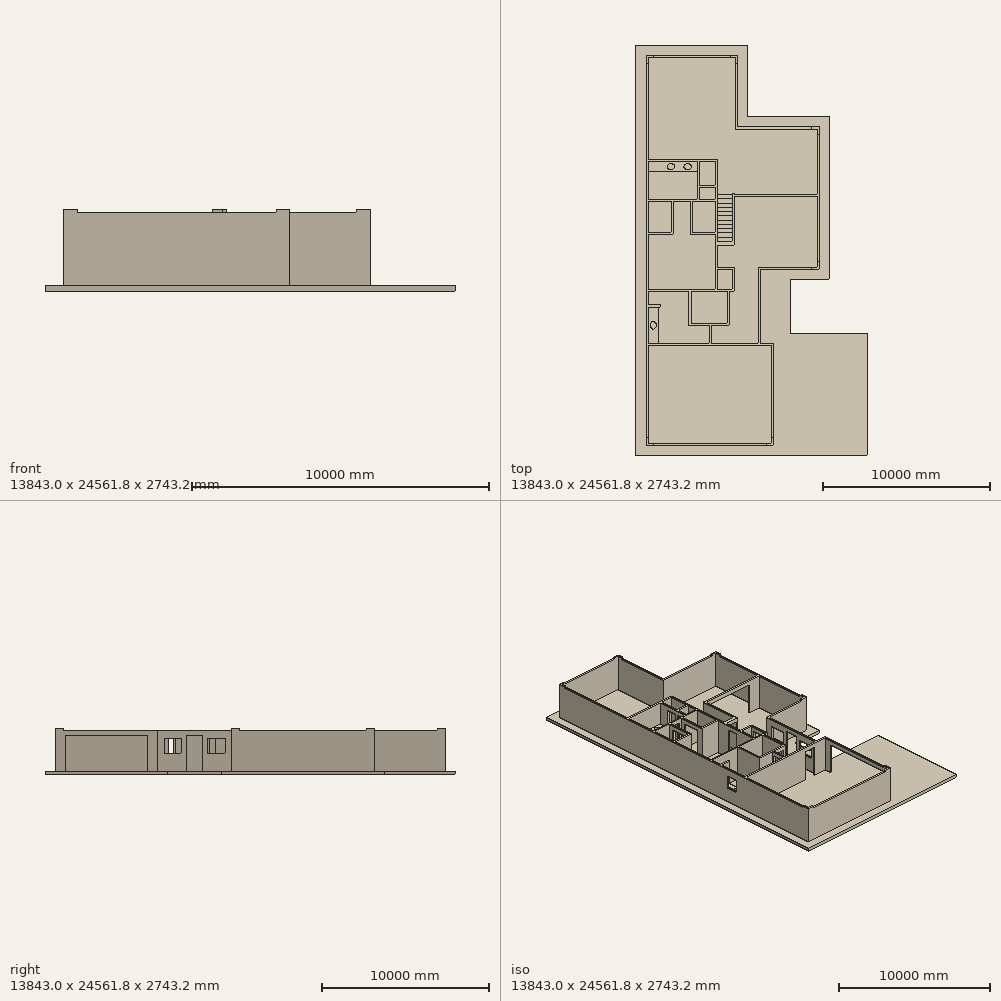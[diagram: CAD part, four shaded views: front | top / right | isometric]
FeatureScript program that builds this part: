
annotation { "Feature Type Name" : "Feature", "Feature Type Description" : "" }
export const myFeature = defineFeature(function(context is Context, id is Id, definition is map)
    precondition{}
    {
        {
            var Q0;
            Q0=qCreatedBy(makeId("Top.planeOp"),FACE);
            var sketch = newSketch(context, id + "F0", { "sketchPlane" : qUnion([Q0])});
            skLineSegment(sketch, "E0", {"start": v(0, 0) * mm, "end": v(7645.4, 0) * mm});
            skLineSegment(sketch, "E1", {"start": v(7645.4, 0) * mm, "end": v(7645.4, 6096) * mm});
            skLineSegment(sketch, "E2", {"start": v(7645.4, 6096) * mm, "end": v(6832.6, 6096) * mm});
            skLineSegment(sketch, "E3", {"start": v(6832.6, 6096) * mm, "end": v(6832.6, 10541) * mm});
            skLineSegment(sketch, "E4", {"start": v(6832.6, 10541) * mm, "end": v(10363.2, 10541) * mm});
            skLineSegment(sketch, "E5", {"start": v(10363.2, 10541) * mm, "end": v(10363.2, 19075.4) * mm});
            skLineSegment(sketch, "E6", {"start": v(10363.2, 19075.4) * mm, "end": v(5486.4, 19075.4) * mm});
            skLineSegment(sketch, "E7", {"start": v(5486.4, 19075.4) * mm, "end": v(5486.4, 23342.6) * mm});
            skLineSegment(sketch, "E8", {"start": v(5486.4, 23342.6) * mm, "end": v(0, 23342.6) * mm});
            skLineSegment(sketch, "E9", {"start": v(0, 23342.6) * mm, "end": v(0, 0) * mm});
            skSolve(sketch);
        }
        {
            var Q0;
            Q0=qSketchRegion(id+"F0",true);
            extrude(context, id + "F1", {"entities" : qUnion([Q0]), "depth" : 2641.6 * mm});
        }
        {
            var Q0;
            Q0=qCreatedBy(makeId("Top.planeOp"),FACE);
            var sketch = newSketch(context, id + "F2", { "sketchPlane" : qUnion([Q0])});
            skLineSegment(sketch, "E10", {"start": v(-609.6, 23952.2) * mm, "end": v(-609.6, -609.6) * mm});
            skLineSegment(sketch, "E11", {"start": v(-609.6, -609.6) * mm, "end": v(13233.4, -609.6) * mm});
            skLineSegment(sketch, "E12", {"start": v(13233.4, -609.6) * mm, "end": v(13233.4, 6705.6) * mm});
            skLineSegment(sketch, "E13", {"start": v(13233.4, 6705.6) * mm, "end": v(8661.4, 6705.6) * mm});
            skLineSegment(sketch, "E14", {"start": v(8661.4, 6705.6) * mm, "end": v(8661.4, 9931.4) * mm});
            skLineSegment(sketch, "E15", {"start": v(8661.4, 9931.4) * mm, "end": v(10972.8, 9931.4) * mm});
            skLineSegment(sketch, "E16", {"start": v(10972.8, 9931.4) * mm, "end": v(10972.8, 19685) * mm});
            skLineSegment(sketch, "E17", {"start": v(10972.8, 19685) * mm, "end": v(6096, 19685) * mm});
            skLineSegment(sketch, "E18", {"start": v(6096, 19685) * mm, "end": v(6096, 23952.2) * mm});
            skLineSegment(sketch, "E19", {"start": v(6096, 23952.2) * mm, "end": v(-609.6, 23952.2) * mm});
            skSolve(sketch);
        }
        {
            var Q0;
            Q0=qSketchRegion(id+"F2",true);
            extrude(context, id + "F3", {"entities" : qUnion([Q0]), "operationType" : NewBodyOperationType.ADD, "depth" : 203.2 * mm});
        }
        {
            var Q0;
            Q0=makeQuery(id+"F1.opExtrude","CAP_FACE",FACE,{"disambiguationData":[OSD([sQuery(id+"F0.wireOp",EDGE,"E0"),sQuery(id+"F0.wireOp",EDGE,"E1"),sQuery(id+"F0.wireOp",EDGE,"E2"),sQuery(id+"F0.wireOp",EDGE,"E3"),sQuery(id+"F0.wireOp",EDGE,"E4"),sQuery(id+"F0.wireOp",EDGE,"E5"),sQuery(id+"F0.wireOp",EDGE,"E6"),sQuery(id+"F0.wireOp",EDGE,"E7"),sQuery(id+"F0.wireOp",EDGE,"E8"),sQuery(id+"F0.wireOp",EDGE,"E9")])],"isStart":false});
            var sketch = newSketch(context, id + "F4", { "sketchPlane" : qUnion([Q0])});
            skLineSegment(sketch, "E20.bottom", {"start": v(127, 23215.6) * mm, "end": v(5359.4, 23215.6) * mm});
            skLineSegment(sketch, "E20.left", {"start": v(127, 23215.6) * mm, "end": v(127, 17119.6) * mm});
            skLineSegment(sketch, "E20.right", {"start": v(5359.4, 23215.6) * mm, "end": v(5359.4, 18948.4) * mm});
            skLineSegment(sketch, "E21.bottom", {"start": v(127, 5969) * mm, "end": v(7518.4, 5969) * mm});
            skLineSegment(sketch, "E21.top", {"start": v(127, 127) * mm, "end": v(7518.4, 127) * mm});
            skLineSegment(sketch, "E21.left", {"start": v(127, 5969) * mm, "end": v(127, 127) * mm});
            skLineSegment(sketch, "E21.right", {"start": v(7518.4, 5969) * mm, "end": v(7518.4, 127) * mm});
            skLineSegment(sketch, "E22", {"start": v(5359.4, 18948.4) * mm, "end": v(10236.2, 18948.4) * mm});
            skLineSegment(sketch, "E23", {"start": v(127, 17119.6) * mm, "end": v(4267.2, 17119.6) * mm});
            skLineSegment(sketch, "E24", {"start": v(4267.2, 17119.6) * mm, "end": v(4267.2, 10668) * mm});
            skLineSegment(sketch, "E25", {"start": v(4267.2, 10668) * mm, "end": v(5308.6, 10668) * mm});
            skLineSegment(sketch, "E26", {"start": v(10236.2, 10668) * mm, "end": v(10236.2, 14884.4) * mm});
            skLineSegment(sketch, "E27", {"start": v(5181.6, 15062.2) * mm, "end": v(5181.6, 11963.4) * mm});
            skLineSegment(sketch, "E28", {"start": v(5181.6, 11963.4) * mm, "end": v(5308.6, 11963.4) * mm});
            skLineSegment(sketch, "E29", {"start": v(5308.6, 11963.4) * mm, "end": v(5308.6, 14884.4) * mm});
            skLineSegment(sketch, "E30", {"start": v(5308.6, 14884.4) * mm, "end": v(10236.2, 14884.4) * mm});
            skLineSegment(sketch, "E31", {"start": v(5181.6, 15062.2) * mm, "end": v(5308.6, 15062.2) * mm});
            skLineSegment(sketch, "E32", {"start": v(5308.6, 15062.2) * mm, "end": v(5308.6, 15011.4) * mm});
            skLineSegment(sketch, "E33", {"start": v(5308.6, 15011.4) * mm, "end": v(10236.2, 15011.4) * mm});
            skLineSegment(sketch, "E34.trimOffspring", {"start": v(10236.2, 15011.4) * mm, "end": v(10236.2, 18948.4) * mm});
            skLineSegment(sketch, "E35.bottom", {"start": v(4140.2, 16992.6) * mm, "end": v(3225.8, 16992.6) * mm});
            skLineSegment(sketch, "E35.top", {"start": v(4140.2, 15570.2) * mm, "end": v(3225.8, 15570.2) * mm});
            skLineSegment(sketch, "E35.left", {"start": v(4140.2, 16992.6) * mm, "end": v(4140.2, 15570.2) * mm});
            skLineSegment(sketch, "E35.right", {"start": v(3225.8, 16992.6) * mm, "end": v(3225.8, 15570.2) * mm});
            skLineSegment(sketch, "E36.bottom", {"start": v(127, 16992.6) * mm, "end": v(3098.8, 16992.6) * mm});
            skLineSegment(sketch, "E36.top", {"start": v(127, 14706.6) * mm, "end": v(3098.8, 14706.6) * mm});
            skLineSegment(sketch, "E36.left", {"start": v(127, 16992.6) * mm, "end": v(127, 14706.6) * mm});
            skLineSegment(sketch, "E36.right", {"start": v(3098.8, 16992.6) * mm, "end": v(3098.8, 14706.6) * mm});
            skLineSegment(sketch, "E37.bottom", {"start": v(127, 14579.6) * mm, "end": v(1498.6, 14579.6) * mm});
            skLineSegment(sketch, "E37.top", {"start": v(127, 12750.8) * mm, "end": v(1498.6, 12750.8) * mm});
            skLineSegment(sketch, "E37.left", {"start": v(127, 14579.6) * mm, "end": v(127, 12750.8) * mm});
            skLineSegment(sketch, "E37.right", {"start": v(1498.6, 14579.6) * mm, "end": v(1498.6, 12750.8) * mm});
            skLineSegment(sketch, "E38.bottom", {"start": v(2768.6, 14579.6) * mm, "end": v(4140.2, 14579.6) * mm});
            skLineSegment(sketch, "E38.top", {"start": v(2768.6, 12750.8) * mm, "end": v(4140.2, 12750.8) * mm});
            skLineSegment(sketch, "E38.left", {"start": v(2768.6, 14579.6) * mm, "end": v(2768.6, 12750.8) * mm});
            skLineSegment(sketch, "E38.right", {"start": v(4140.2, 14579.6) * mm, "end": v(4140.2, 12750.8) * mm});
            skLineSegment(sketch, "E39", {"start": v(2641.6, 12623.8) * mm, "end": v(2641.6, 14579.6) * mm});
            skLineSegment(sketch, "E40", {"start": v(2641.6, 14579.6) * mm, "end": v(1625.6, 14579.6) * mm});
            skLineSegment(sketch, "E41", {"start": v(1625.6, 14579.6) * mm, "end": v(1625.6, 12623.8) * mm});
            skLineSegment(sketch, "E42", {"start": v(1625.6, 12623.8) * mm, "end": v(127, 12623.8) * mm});
            skLineSegment(sketch, "E43", {"start": v(2641.6, 12623.8) * mm, "end": v(4140.2, 12623.8) * mm});
            skLineSegment(sketch, "E44.bottom", {"start": v(4267.2, 10541) * mm, "end": v(5181.6, 10541) * mm});
            skLineSegment(sketch, "E44.top", {"start": v(4267.2, 9321.8) * mm, "end": v(5181.6, 9321.8) * mm});
            skLineSegment(sketch, "E44.left", {"start": v(4267.2, 10541) * mm, "end": v(4267.2, 9321.8) * mm});
            skLineSegment(sketch, "E44.right", {"start": v(5181.6, 10541) * mm, "end": v(5181.6, 9321.8) * mm});
            skLineSegment(sketch, "E45.right", {"start": v(2692.4, 9194.8) * mm, "end": v(2692.4, 7289.8) * mm});
            skLineSegment(sketch, "E46", {"start": v(4140.2, 12623.8) * mm, "end": v(4140.2, 9321.8) * mm});
            skLineSegment(sketch, "E47", {"start": v(4140.2, 9321.8) * mm, "end": v(127, 9321.8) * mm});
            skLineSegment(sketch, "E48", {"start": v(127, 9321.8) * mm, "end": v(127, 12623.8) * mm});
            skLineSegment(sketch, "E49", {"start": v(3784.6, 6096) * mm, "end": v(127, 6096) * mm});
            skLineSegment(sketch, "E50", {"start": v(127, 6096) * mm, "end": v(127, 8280.4) * mm});
            skLineSegment(sketch, "E51", {"start": v(127, 9194.8) * mm, "end": v(2565.4, 9194.8) * mm});
            skLineSegment(sketch, "E52", {"start": v(2565.4, 9194.8) * mm, "end": v(2565.4, 7162.8) * mm});
            skLineSegment(sketch, "E53", {"start": v(2565.4, 7162.8) * mm, "end": v(3784.6, 7162.8) * mm});
            skLineSegment(sketch, "E54", {"start": v(3784.6, 7162.8) * mm, "end": v(3784.6, 6096) * mm});
            skLineSegment(sketch, "E55", {"start": v(3911.6, 7162.8) * mm, "end": v(3911.6, 6096) * mm});
            skLineSegment(sketch, "E56", {"start": v(3911.6, 6096) * mm, "end": v(6705.6, 6096) * mm});
            skLineSegment(sketch, "E57", {"start": v(6705.6, 6096) * mm, "end": v(6705.6, 10668) * mm});
            skLineSegment(sketch, "E58", {"start": v(3911.6, 7162.8) * mm, "end": v(5003.8, 7162.8) * mm});
            skLineSegment(sketch, "E59", {"start": v(5308.6, 9194.8) * mm, "end": v(5308.6, 10668) * mm});
            skLineSegment(sketch, "E60.trimOffspring", {"start": v(6705.6, 10668) * mm, "end": v(10236.2, 10668) * mm});
            skLineSegment(sketch, "E61.bottom", {"start": v(3225.8, 15443.2) * mm, "end": v(4140.2, 15443.2) * mm});
            skLineSegment(sketch, "E61.top", {"start": v(3225.8, 14706.6) * mm, "end": v(4140.2, 14706.6) * mm});
            skLineSegment(sketch, "E61.left", {"start": v(3225.8, 15443.2) * mm, "end": v(3225.8, 14706.6) * mm});
            skLineSegment(sketch, "E61.right", {"start": v(4140.2, 15443.2) * mm, "end": v(4140.2, 14706.6) * mm});
            skLineSegment(sketch, "E62", {"start": v(127, 8407.4) * mm, "end": v(889, 8407.4) * mm});
            skLineSegment(sketch, "E63", {"start": v(889, 8407.4) * mm, "end": v(889, 8280.4) * mm});
            skLineSegment(sketch, "E64", {"start": v(889, 8280.4) * mm, "end": v(127, 8280.4) * mm});
            skLineSegment(sketch, "E65.trimOffspring", {"start": v(127, 8407.4) * mm, "end": v(127, 9194.8) * mm});
            skLineSegment(sketch, "E66", {"start": v(2692.4, 9194.8) * mm, "end": v(4876.8, 9194.8) * mm});
            skLineSegment(sketch, "E67", {"start": v(4876.8, 9194.8) * mm, "end": v(4876.8, 7289.8) * mm});
            skLineSegment(sketch, "E68", {"start": v(4876.8, 7289.8) * mm, "end": v(2692.4, 7289.8) * mm});
            skLineSegment(sketch, "E69", {"start": v(5003.8, 7162.8) * mm, "end": v(5003.8, 9194.8) * mm});
            skLineSegment(sketch, "E70", {"start": v(5003.8, 9194.8) * mm, "end": v(5308.6, 9194.8) * mm});
            skSolve(sketch);
        }
        {
            var Q0;
            Q0=qSketchRegion(id+"F4",true);
            extrude(context, id + "F5", {"entities" : qUnion([Q0]), "operationType" : NewBodyOperationType.REMOVE, "oppositeDirection" : true, "depth" : 2438.4 * mm});
        }
        {
            var Q0;
            Q0=makeQuery(id+"F5.boolean.opBoolean","COPY",FACE,{"derivedFrom":makeQuery(id+"F5.opExtrude","SWEPT_FACE",FACE,{"disambiguationData":[OSD([sQuery(id+"F4.wireOp",EDGE,"E24")])]})});
            var sketch = newSketch(context, id + "F6", { "sketchPlane" : qUnion([Q0])});
            skLineSegment(sketch, "E71", {"start": v(14757.4, 203.2) * mm, "end": v(15011.4, 203.2) * mm});
            skLineSegment(sketch, "E72", {"start": v(15011.4, 203.2) * mm, "end": v(15011.4, 406.4) * mm});
            skLineSegment(sketch, "E73", {"start": v(15011.4, 406.4) * mm, "end": v(14757.4, 406.4) * mm});
            skLineSegment(sketch, "E74", {"start": v(14757.4, 406.4) * mm, "end": v(14757.4, 609.6) * mm});
            skLineSegment(sketch, "E75", {"start": v(14757.4, 609.6) * mm, "end": v(14503.4, 609.6) * mm});
            skLineSegment(sketch, "E76", {"start": v(14503.4, 609.6) * mm, "end": v(14503.4, 812.8) * mm});
            skLineSegment(sketch, "E77", {"start": v(14503.4, 812.8) * mm, "end": v(14249.4, 812.8) * mm});
            skLineSegment(sketch, "E78", {"start": v(14249.4, 812.8) * mm, "end": v(14249.4, 1016) * mm});
            skLineSegment(sketch, "E79", {"start": v(14249.4, 1016) * mm, "end": v(13995.4, 1016) * mm});
            skLineSegment(sketch, "E80", {"start": v(13995.4, 1016) * mm, "end": v(13995.4, 1219.2) * mm});
            skLineSegment(sketch, "E81", {"start": v(13995.4, 1219.2) * mm, "end": v(13741.4, 1219.2) * mm});
            skLineSegment(sketch, "E82", {"start": v(13741.4, 1219.2) * mm, "end": v(13741.4, 1422.4) * mm});
            skLineSegment(sketch, "E83", {"start": v(13741.4, 1422.4) * mm, "end": v(13487.4, 1422.4) * mm});
            skLineSegment(sketch, "E84", {"start": v(13487.4, 1422.4) * mm, "end": v(13487.4, 1625.6) * mm});
            skLineSegment(sketch, "E85", {"start": v(13487.4, 1625.6) * mm, "end": v(13233.4, 1625.6) * mm});
            skLineSegment(sketch, "E86", {"start": v(13233.4, 1625.6) * mm, "end": v(13233.4, 1828.8) * mm});
            skLineSegment(sketch, "E87", {"start": v(13233.4, 1828.8) * mm, "end": v(12979.4, 1828.8) * mm});
            skLineSegment(sketch, "E88", {"start": v(12979.4, 1828.8) * mm, "end": v(12979.4, 2032) * mm});
            skLineSegment(sketch, "E89", {"start": v(12979.4, 2032) * mm, "end": v(12725.4, 2032) * mm});
            skLineSegment(sketch, "E90", {"start": v(12725.4, 2032) * mm, "end": v(12725.4, 2235.2) * mm});
            skLineSegment(sketch, "E91", {"start": v(12725.4, 2235.2) * mm, "end": v(12471.4, 2235.2) * mm});
            skLineSegment(sketch, "E92", {"start": v(12471.4, 2235.2) * mm, "end": v(12471.4, 2438.4) * mm});
            skLineSegment(sketch, "E93", {"start": v(12471.4, 2438.4) * mm, "end": v(12217.4, 2438.4) * mm});
            skLineSegment(sketch, "E94", {"start": v(12217.4, 2438.4) * mm, "end": v(12217.4, 2641.6) * mm});
            skLineSegment(sketch, "E95", {"start": v(12217.4, 2641.6) * mm, "end": v(11963.4, 2641.6) * mm});
            skLineSegment(sketch, "E96", {"start": v(11963.4, 2641.6) * mm, "end": v(11963.4, 2387.6) * mm});
            skLineSegment(sketch, "E97", {"start": v(11963.4, 2387.6) * mm, "end": v(14757.4, 203.2) * mm});
            skSolve(sketch);
        }
        {
            var Q0;
            Q0=qSketchRegion(id+"F6",true);
            extrude(context, id + "F7", {"entities" : qUnion([Q0]), "operationType" : NewBodyOperationType.ADD, "endBound" : BoundingType.UP_TO_NEXT, "depth" : 25.4 * mm});
        }
        {
            var Q0;
            Q0=makeQuery(id+"F5.boolean.opBoolean","COPY",FACE,{"derivedFrom":makeQuery(id+"F5.opExtrude","SWEPT_FACE",FACE,{"disambiguationData":[OSD([sQuery(id+"F4.wireOp",EDGE,"E21.right")])]})});
            var sketch = newSketch(context, id + "F8", { "sketchPlane" : qUnion([Q0])});
            skLineSegment(sketch, "E98.bottom", {"start": v(-5486.4, 203.2) * mm, "end": v(-609.6, 203.2) * mm});
            skLineSegment(sketch, "E98.top", {"start": v(-5486.4, 2336.8) * mm, "end": v(-609.6, 2336.8) * mm});
            skLineSegment(sketch, "E98.left", {"start": v(-5486.4, 203.2) * mm, "end": v(-5486.4, 2336.8) * mm});
            skLineSegment(sketch, "E98.right", {"start": v(-609.6, 203.2) * mm, "end": v(-609.6, 2336.8) * mm});
            skLineSegment(sketch, "E99", {"start": v(-3048, 2641.6) * mm, "end": v(-3048, 203.2) * mm, "construction": true});
            skSolve(sketch);
        }
        {
            var Q0;
            Q0=qSketchRegion(id+"F8",true);
            extrude(context, id + "F9", {"entities" : qUnion([Q0]), "operationType" : NewBodyOperationType.REMOVE, "endBound" : BoundingType.UP_TO_NEXT, "oppositeDirection" : true, "depth" : 25.4 * mm});
        }
        {
            var Q0;
            Q0=makeQuery(id+"F5.boolean.opBoolean","COPY",FACE,{"derivedFrom":makeQuery(id+"F5.opExtrude","SWEPT_FACE",FACE,{"disambiguationData":[OSD([sQuery(id+"F4.wireOp",EDGE,"E30")])]})});
            var sketch = newSketch(context, id + "F10", { "sketchPlane" : qUnion([Q0])});
            skLineSegment(sketch, "E100.bottom", {"start": v(5461, 203.2) * mm, "end": v(9372.6, 203.2) * mm});
            skLineSegment(sketch, "E100.top", {"start": v(5461, 2336.8) * mm, "end": v(9372.6, 2336.8) * mm});
            skLineSegment(sketch, "E100.left", {"start": v(5461, 203.2) * mm, "end": v(5461, 2336.8) * mm});
            skLineSegment(sketch, "E100.right", {"start": v(9372.6, 203.2) * mm, "end": v(9372.6, 2336.8) * mm});
            skSolve(sketch);
        }
        {
            var Q0;
            Q0=qSketchRegion(id+"F10",true);
            extrude(context, id + "F11", {"entities" : qUnion([Q0]), "operationType" : NewBodyOperationType.REMOVE, "endBound" : BoundingType.UP_TO_NEXT, "oppositeDirection" : true, "depth" : 25.4 * mm});
        }
        {
            var Q0;
            Q0=makeQuery(id+"F5.boolean.opBoolean","COPY",FACE,{"derivedFrom":makeQuery(id+"F5.opExtrude","CAP_FACE",FACE,{"disambiguationData":[OSD([sQuery(id+"F4.wireOp",EDGE,"E36.bottom"),sQuery(id+"F4.wireOp",EDGE,"E36.top"),sQuery(id+"F4.wireOp",EDGE,"E36.left"),sQuery(id+"F4.wireOp",EDGE,"E36.right")])],"isStart":false})});
            var sketch = newSketch(context, id + "F12", { "sketchPlane" : qUnion([Q0])});
            skLineSegment(sketch, "E101.bottom", {"start": v(127, 16992.6) * mm, "end": v(3098.8, 16992.6) * mm});
            skLineSegment(sketch, "E101.top", {"start": v(127, 16383) * mm, "end": v(3098.8, 16383) * mm});
            skLineSegment(sketch, "E101.left", {"start": v(127, 16992.6) * mm, "end": v(127, 16383) * mm});
            skLineSegment(sketch, "E101.right", {"start": v(3098.8, 16992.6) * mm, "end": v(3098.8, 16383) * mm});
            skSolve(sketch);
        }
        {
            var Q0;
            Q0=qSketchRegion(id+"F12",true);
            extrude(context, id + "F13", {"entities" : qUnion([Q0]), "operationType" : NewBodyOperationType.ADD, "depth" : 838.2 * mm});
        }
        {
            var Q0;
            Q0=makeQuery(id+"F13.opExtrude","CAP_FACE",FACE,{"disambiguationData":[OSD([sQuery(id+"F12.wireOp",EDGE,"E101.bottom"),sQuery(id+"F12.wireOp",EDGE,"E101.top"),sQuery(id+"F12.wireOp",EDGE,"E101.left"),sQuery(id+"F12.wireOp",EDGE,"E101.right")])],"isStart":false});
            var sketch = newSketch(context, id + "F14", { "sketchPlane" : qUnion([Q0])});
            skLineSegment(sketch, "E102", {"start": v(2489.2, 16992.6) * mm, "end": v(2489.2, 16383) * mm, "construction": true});
            skLineSegment(sketch, "E103", {"start": v(1498.6, 16992.6) * mm, "end": v(1498.6, 16383) * mm, "construction": true});
            skEllipse(sketch, "E104", {"center": v(2489.2, 16687.8) * mm, "majorRadius": 228.6 * mm, "minorRadius": 177.8 * mm, "majorAxis": v(-1, 0)});
            skEllipse(sketch, "E105", {"center": v(1498.6, 16687.8) * mm, "majorRadius": 228.6 * mm, "minorRadius": 177.8 * mm, "majorAxis": v(-1, 0)});
            skSolve(sketch);
        }
        {
            var Q0;
            Q0=qSketchRegion(id+"F14",true);
            extrude(context, id + "F15", {"entities" : qUnion([Q0]), "operationType" : NewBodyOperationType.REMOVE, "oppositeDirection" : true, "depth" : 304.8 * mm});
        }
        {
            var Q0;
            Q0=makeQuery(id+"F5.boolean.opBoolean","COPY",FACE,{"derivedFrom":makeQuery(id+"F5.opExtrude","CAP_FACE",FACE,{"disambiguationData":[OSD([sQuery(id+"F4.wireOp",EDGE,"E49"),sQuery(id+"F4.wireOp",EDGE,"E50"),sQuery(id+"F4.wireOp",EDGE,"E51"),sQuery(id+"F4.wireOp",EDGE,"E52"),sQuery(id+"F4.wireOp",EDGE,"E53"),sQuery(id+"F4.wireOp",EDGE,"E54")])],"isStart":false})});
            var sketch = newSketch(context, id + "F16", { "sketchPlane" : qUnion([Q0])});
            skLineSegment(sketch, "E106.bottom", {"start": v(127, 6096) * mm, "end": v(736.6, 6096) * mm});
            skLineSegment(sketch, "E106.top", {"start": v(127, 8280.4) * mm, "end": v(736.6, 8280.4) * mm});
            skLineSegment(sketch, "E106.left", {"start": v(127, 6096) * mm, "end": v(127, 8280.4) * mm});
            skLineSegment(sketch, "E106.right", {"start": v(736.6, 6096) * mm, "end": v(736.6, 8280.4) * mm});
            skSolve(sketch);
        }
        {
            var Q0;
            Q0=qSketchRegion(id+"F16",true);
            extrude(context, id + "F17", {"entities" : qUnion([Q0]), "operationType" : NewBodyOperationType.ADD, "depth" : 838.2 * mm});
        }
        {
            var Q0;
            Q0=makeQuery(id+"F17.opExtrude","CAP_FACE",FACE,{"disambiguationData":[OSD([sQuery(id+"F16.wireOp",EDGE,"E106.bottom"),sQuery(id+"F16.wireOp",EDGE,"E106.top"),sQuery(id+"F16.wireOp",EDGE,"E106.left"),sQuery(id+"F16.wireOp",EDGE,"E106.right")])],"isStart":false});
            var sketch = newSketch(context, id + "F18", { "sketchPlane" : qUnion([Q0])});
            skLineSegment(sketch, "E107", {"start": v(127, 7188.2) * mm, "end": v(736.6, 7188.2) * mm, "construction": true});
            skEllipse(sketch, "E108", {"center": v(431.8, 7188.2) * mm, "majorRadius": 228.6 * mm, "minorRadius": 177.8 * mm, "majorAxis": v(0, 1)});
            skSolve(sketch);
        }
        {
            var Q0;
            Q0=qSketchRegion(id+"F18",true);
            extrude(context, id + "F19", {"entities" : qUnion([Q0]), "operationType" : NewBodyOperationType.REMOVE, "oppositeDirection" : true, "depth" : 304.8 * mm});
        }
        {
            var Q0;
            Q0=makeQuery(id+"F1.opExtrude","SWEPT_FACE",FACE,{"disambiguationData":[OSD([sQuery(id+"F0.wireOp",EDGE,"E3")])]});
            var sketch = newSketch(context, id + "F20", { "sketchPlane" : qUnion([Q0])});
            skLineSegment(sketch, "E109.bottom", {"start": v(7861.3, 203.2) * mm, "end": v(8775.7, 203.2) * mm});
            skLineSegment(sketch, "E109.top", {"start": v(7861.3, 2336.8) * mm, "end": v(8775.7, 2336.8) * mm});
            skLineSegment(sketch, "E109.left", {"start": v(7861.3, 203.2) * mm, "end": v(7861.3, 2336.8) * mm});
            skLineSegment(sketch, "E109.right", {"start": v(8775.7, 203.2) * mm, "end": v(8775.7, 2336.8) * mm});
            skLineSegment(sketch, "E110", {"start": v(8318.5, 2641.6) * mm, "end": v(8318.5, 203.2) * mm, "construction": true});
            skLineSegment(sketch, "E111.bottom", {"start": v(6489.7, 2159) * mm, "end": v(7556.5, 2159) * mm});
            skLineSegment(sketch, "E111.top", {"start": v(6489.7, 1244.6) * mm, "end": v(7556.5, 1244.6) * mm});
            skLineSegment(sketch, "E111.left", {"start": v(6489.7, 2159) * mm, "end": v(6489.7, 1244.6) * mm});
            skLineSegment(sketch, "E111.right", {"start": v(7556.5, 2159) * mm, "end": v(7556.5, 1244.6) * mm});
            skLineSegment(sketch, "E112.MirrorCS", {"start": v(10147.3, 2159) * mm, "end": v(9080.5, 2159) * mm});
            skLineSegment(sketch, "E113.MirrorCS", {"start": v(10147.3, 1244.6) * mm, "end": v(9080.5, 1244.6) * mm});
            skLineSegment(sketch, "E114.MirrorCS", {"start": v(10147.3, 2159) * mm, "end": v(10147.3, 1244.6) * mm});
            skLineSegment(sketch, "E115.MirrorCS", {"start": v(9080.5, 2159) * mm, "end": v(9080.5, 1244.6) * mm});
            skSolve(sketch);
        }
        {
            var Q0;
            Q0=qSketchRegion(id+"F20",true);
            extrude(context, id + "F21", {"entities" : qUnion([Q0]), "operationType" : NewBodyOperationType.REMOVE, "endBound" : BoundingType.UP_TO_NEXT, "oppositeDirection" : true, "depth" : 25.4 * mm});
        }
        {
            var Q0;
            Q0=makeQuery(id+"F5.boolean.opBoolean","COPY",FACE,{"derivedFrom":makeQuery(id+"F5.opExtrude","SWEPT_FACE",FACE,{"disambiguationData":[OSD([sQuery(id+"F4.wireOp",EDGE,"E56")])]})});
            var sketch = newSketch(context, id + "F22", { "sketchPlane" : qUnion([Q0])});
            skLineSegment(sketch, "E116.bottom", {"start": v(-6553.2, 203.2) * mm, "end": v(-5638.8, 203.2) * mm});
            skLineSegment(sketch, "E116.top", {"start": v(-6553.2, 2336.8) * mm, "end": v(-5638.8, 2336.8) * mm});
            skLineSegment(sketch, "E116.left", {"start": v(-6553.2, 203.2) * mm, "end": v(-6553.2, 2336.8) * mm});
            skLineSegment(sketch, "E116.right", {"start": v(-5638.8, 203.2) * mm, "end": v(-5638.8, 2336.8) * mm});
            skSolve(sketch);
        }
        {
            var Q0;
            Q0=qSketchRegion(id+"F22",true);
            extrude(context, id + "F23", {"entities" : qUnion([Q0]), "operationType" : NewBodyOperationType.REMOVE, "endBound" : BoundingType.UP_TO_NEXT, "oppositeDirection" : true, "depth" : 25.4 * mm});
        }
        {
            var Q0;
            Q0=makeQuery(id+"F5.boolean.opBoolean","COPY",FACE,{"derivedFrom":makeQuery(id+"F5.opExtrude","SWEPT_FACE",FACE,{"disambiguationData":[OSD([sQuery(id+"F4.wireOp",EDGE,"E58")])]})});
            var sketch = newSketch(context, id + "F24", { "sketchPlane" : qUnion([Q0])});
            skLineSegment(sketch, "E117.bottom", {"start": v(4013.2, 203.2) * mm, "end": v(4775.2, 203.2) * mm});
            skLineSegment(sketch, "E117.top", {"start": v(4013.2, 2336.8) * mm, "end": v(4775.2, 2336.8) * mm});
            skLineSegment(sketch, "E117.left", {"start": v(4013.2, 203.2) * mm, "end": v(4013.2, 2336.8) * mm});
            skLineSegment(sketch, "E117.right", {"start": v(4775.2, 203.2) * mm, "end": v(4775.2, 2336.8) * mm});
            skSolve(sketch);
        }
        {
            var Q0;
            Q0=qSketchRegion(id+"F24",true);
            extrude(context, id + "F25", {"entities" : qUnion([Q0]), "operationType" : NewBodyOperationType.REMOVE, "endBound" : BoundingType.UP_TO_NEXT, "oppositeDirection" : true, "depth" : 25.4 * mm});
        }
        {
            var Q0;
            Q0=makeQuery(id+"F5.boolean.opBoolean","COPY",FACE,{"derivedFrom":makeQuery(id+"F5.opExtrude","SWEPT_FACE",FACE,{"disambiguationData":[OSD([sQuery(id+"F4.wireOp",EDGE,"E55")])]})});
            var sketch = newSketch(context, id + "F26", { "sketchPlane" : qUnion([Q0])});
            skLineSegment(sketch, "E118.bottom", {"start": v(7048.5, 203.2) * mm, "end": v(6286.5, 203.2) * mm});
            skLineSegment(sketch, "E118.top", {"start": v(7048.5, 2336.8) * mm, "end": v(6286.5, 2336.8) * mm});
            skLineSegment(sketch, "E118.left", {"start": v(7048.5, 203.2) * mm, "end": v(7048.5, 2336.8) * mm});
            skLineSegment(sketch, "E118.right", {"start": v(6286.5, 203.2) * mm, "end": v(6286.5, 2336.8) * mm});
            skSolve(sketch);
        }
        {
            var Q0;
            Q0=qSketchRegion(id+"F26",true);
            extrude(context, id + "F27", {"entities" : qUnion([Q0]), "operationType" : NewBodyOperationType.REMOVE, "endBound" : BoundingType.UP_TO_NEXT, "oppositeDirection" : true, "depth" : 25.4 * mm});
        }
        {
            var Q0;
            Q0=makeQuery(id+"F5.boolean.opBoolean","COPY",FACE,{"derivedFrom":makeQuery(id+"F5.opExtrude","SWEPT_FACE",FACE,{"disambiguationData":[OSD([sQuery(id+"F4.wireOp",EDGE,"E50")])]})});
            var sketch = newSketch(context, id + "F28", { "sketchPlane" : qUnion([Q0])});
            skLineSegment(sketch, "E119.bottom", {"start": v(6731, 2159) * mm, "end": v(7645.4, 2159) * mm});
            skLineSegment(sketch, "E119.top", {"start": v(6731, 1244.6) * mm, "end": v(7645.4, 1244.6) * mm});
            skLineSegment(sketch, "E119.left", {"start": v(6731, 2159) * mm, "end": v(6731, 1244.6) * mm});
            skLineSegment(sketch, "E119.right", {"start": v(7645.4, 2159) * mm, "end": v(7645.4, 1244.6) * mm});
            skLineSegment(sketch, "E120", {"start": v(7188.2, 2641.6) * mm, "end": v(7188.2, 1041.4) * mm, "construction": true});
            skSolve(sketch);
        }
        {
            var Q0;
            Q0=qSketchRegion(id+"F28",true);
            extrude(context, id + "F29", {"entities" : qUnion([Q0]), "operationType" : NewBodyOperationType.REMOVE, "endBound" : BoundingType.UP_TO_NEXT, "oppositeDirection" : true, "depth" : 25.4 * mm});
        }
        {
            var Q0;
            Q0=makeQuery(id+"F5.boolean.opBoolean","COPY",FACE,{"derivedFrom":makeQuery(id+"F5.opExtrude","SWEPT_FACE",FACE,{"disambiguationData":[OSD([sQuery(id+"F4.wireOp",EDGE,"E59")])]})});
            var sketch = newSketch(context, id + "F30", { "sketchPlane" : qUnion([Q0])});
            skLineSegment(sketch, "E121.bottom", {"start": v(9550.4, 203.2) * mm, "end": v(10312.4, 203.2) * mm});
            skLineSegment(sketch, "E121.top", {"start": v(9550.4, 2336.8) * mm, "end": v(10312.4, 2336.8) * mm});
            skLineSegment(sketch, "E121.left", {"start": v(9550.4, 203.2) * mm, "end": v(9550.4, 2336.8) * mm});
            skLineSegment(sketch, "E121.right", {"start": v(10312.4, 203.2) * mm, "end": v(10312.4, 2336.8) * mm});
            skSolve(sketch);
        }
        {
            var Q0;
            Q0=qSketchRegion(id+"F30",true);
            extrude(context, id + "F31", {"entities" : qUnion([Q0]), "operationType" : NewBodyOperationType.REMOVE, "endBound" : BoundingType.UP_TO_NEXT, "oppositeDirection" : true, "depth" : 25.4 * mm});
        }
        {
            var Q0;
            {var subQ0=sQuery(id+"F4.wireOp",EDGE,"E25");var subQ2=sQuery(id+"F4.wireOp",EDGE,"E24");Q0=makeQuery(id+"F7.boolean.opBoolean","SPLIT",FACE,{"disambiguationData":[TD([makeQuery(id+"F5.boolean.opBoolean","COPY",FACE,{"derivedFrom":makeQuery(id+"F5.opExtrude","SWEPT_FACE",FACE,{"disambiguationData":[OSD([subQ0])]})})])],"derivedFrom":makeQuery(id+"F5.boolean.opBoolean","COPY",FACE,{"derivedFrom":makeQuery(id+"F5.opExtrude","SWEPT_FACE",FACE,{"disambiguationData":[OSD([subQ2])]})})});}
            var sketch = newSketch(context, id + "F32", { "sketchPlane" : qUnion([Q0])});
            skLineSegment(sketch, "E122.bottom", {"start": v(10922, 203.2) * mm, "end": v(11684, 203.2) * mm});
            skLineSegment(sketch, "E122.top", {"start": v(10922, 2336.8) * mm, "end": v(11684, 2336.8) * mm});
            skLineSegment(sketch, "E122.left", {"start": v(10922, 203.2) * mm, "end": v(10922, 2336.8) * mm});
            skLineSegment(sketch, "E122.right", {"start": v(11684, 203.2) * mm, "end": v(11684, 2336.8) * mm});
            skSolve(sketch);
        }
        {
            var Q0;
            Q0=qSketchRegion(id+"F32",true);
            extrude(context, id + "F33", {"entities" : qUnion([Q0]), "operationType" : NewBodyOperationType.REMOVE, "endBound" : BoundingType.UP_TO_NEXT, "oppositeDirection" : true, "depth" : 25.4 * mm});
        }
        {
            var Q0;
            Q0=makeQuery(id+"F5.boolean.opBoolean","COPY",FACE,{"derivedFrom":makeQuery(id+"F5.opExtrude","SWEPT_FACE",FACE,{"disambiguationData":[OSD([sQuery(id+"F4.wireOp",EDGE,"E38.left")])]})});
            var sketch = newSketch(context, id + "F34", { "sketchPlane" : qUnion([Q0])});
            skLineSegment(sketch, "E123", {"start": v(13665.2, 2641.6) * mm, "end": v(13665.2, 203.2) * mm, "construction": true});
            skLineSegment(sketch, "E124.bottom", {"start": v(14274.8, 203.2) * mm, "end": v(13055.6, 203.2) * mm});
            skLineSegment(sketch, "E124.top", {"start": v(14274.8, 2336.8) * mm, "end": v(13055.6, 2336.8) * mm});
            skLineSegment(sketch, "E124.left", {"start": v(14274.8, 203.2) * mm, "end": v(14274.8, 2336.8) * mm});
            skLineSegment(sketch, "E124.right", {"start": v(13055.6, 203.2) * mm, "end": v(13055.6, 2336.8) * mm});
            skSolve(sketch);
        }
        {
            var Q0;
            Q0=qSketchRegion(id+"F34",true);
            var Q1;
            Q1=makeQuery(id+"F5.boolean.opBoolean","COPY",FACE,{"derivedFrom":makeQuery(id+"F5.opExtrude","SWEPT_FACE",FACE,{"disambiguationData":[OSD([sQuery(id+"F4.wireOp",EDGE,"E37.right")])]})});
            extrude(context, id + "F35", {"entities" : qUnion([Q0]), "operationType" : NewBodyOperationType.REMOVE, "endBound" : BoundingType.UP_TO_SURFACE, "oppositeDirection" : true, "endBoundEntityFace" : qUnion([Q1]), "depth" : 25.4 * mm});
        }
        {
            var Q0;
            Q0=makeQuery(id+"F5.boolean.opBoolean","COPY",FACE,{"derivedFrom":makeQuery(id+"F5.opExtrude","SWEPT_FACE",FACE,{"disambiguationData":[OSD([sQuery(id+"F4.wireOp",EDGE,"E40")])]})});
            var sketch = newSketch(context, id + "F36", { "sketchPlane" : qUnion([Q0])});
            skLineSegment(sketch, "E125", {"start": v(2133.6, 203.2) * mm, "end": v(2133.6, 2641.6) * mm, "construction": true});
            skLineSegment(sketch, "E126.bottom", {"start": v(1752.6, 203.2) * mm, "end": v(2514.6, 203.2) * mm});
            skLineSegment(sketch, "E126.top", {"start": v(1752.6, 2336.8) * mm, "end": v(2514.6, 2336.8) * mm});
            skLineSegment(sketch, "E126.left", {"start": v(1752.6, 203.2) * mm, "end": v(1752.6, 2336.8) * mm});
            skLineSegment(sketch, "E126.right", {"start": v(2514.6, 203.2) * mm, "end": v(2514.6, 2336.8) * mm});
            skSolve(sketch);
        }
        {
            var Q0;
            Q0=qSketchRegion(id+"F36",true);
            extrude(context, id + "F37", {"entities" : qUnion([Q0]), "operationType" : NewBodyOperationType.REMOVE, "endBound" : BoundingType.UP_TO_NEXT, "oppositeDirection" : true, "depth" : 25.4 * mm});
        }
        {
            var Q0;
            Q0=makeQuery(id+"F5.boolean.opBoolean","COPY",FACE,{"derivedFrom":makeQuery(id+"F5.opExtrude","SWEPT_FACE",FACE,{"disambiguationData":[OSD([sQuery(id+"F4.wireOp",EDGE,"E36.right")])]})});
            var sketch = newSketch(context, id + "F38", { "sketchPlane" : qUnion([Q0])});
            skLineSegment(sketch, "E127.bottom", {"start": v(-15621, 203.2) * mm, "end": v(-16281.4, 203.2) * mm});
            skLineSegment(sketch, "E127.top", {"start": v(-15621, 2336.8) * mm, "end": v(-16281.4, 2336.8) * mm});
            skLineSegment(sketch, "E127.left", {"start": v(-15621, 203.2) * mm, "end": v(-15621, 2336.8) * mm});
            skLineSegment(sketch, "E127.right", {"start": v(-16281.4, 203.2) * mm, "end": v(-16281.4, 2336.8) * mm});
            skLineSegment(sketch, "E128.bottom", {"start": v(-15379.7, 203.2) * mm, "end": v(-14770.1, 203.2) * mm});
            skLineSegment(sketch, "E128.top", {"start": v(-15379.7, 2336.8) * mm, "end": v(-14770.1, 2336.8) * mm});
            skLineSegment(sketch, "E128.left", {"start": v(-15379.7, 203.2) * mm, "end": v(-15379.7, 2336.8) * mm});
            skLineSegment(sketch, "E128.right", {"start": v(-14770.1, 203.2) * mm, "end": v(-14770.1, 2336.8) * mm});
            skSolve(sketch);
        }
        {
            var Q0;
            Q0=qSketchRegion(id+"F38",true);
            extrude(context, id + "F39", {"entities" : qUnion([Q0]), "operationType" : NewBodyOperationType.REMOVE, "endBound" : BoundingType.UP_TO_NEXT, "oppositeDirection" : true, "depth" : 25.4 * mm});
        }
        {
            var Q0;
            Q0=makeQuery(id+"F7.boolean.opBoolean","MERGE",FACE,{"derivedFrom":[makeQuery(id+"F1.opExtrude","CAP_FACE",FACE,{"disambiguationData":[OSD([sQuery(id+"F0.wireOp",EDGE,"E0"),sQuery(id+"F0.wireOp",EDGE,"E1"),sQuery(id+"F0.wireOp",EDGE,"E2"),sQuery(id+"F0.wireOp",EDGE,"E3"),sQuery(id+"F0.wireOp",EDGE,"E4"),sQuery(id+"F0.wireOp",EDGE,"E5"),sQuery(id+"F0.wireOp",EDGE,"E6"),sQuery(id+"F0.wireOp",EDGE,"E7"),sQuery(id+"F0.wireOp",EDGE,"E8"),sQuery(id+"F0.wireOp",EDGE,"E9")])],"isStart":false}),makeQuery(id+"F7.opExtrude","SWEPT_FACE",FACE,{"disambiguationData":[OSD([sQuery(id+"F6.wireOp",EDGE,"E95")])]})]});
            var sketch = newSketch(context, id + "F40", { "sketchPlane" : qUnion([Q0])});
            skLineSegment(sketch, "E129", {"start": v(0, 0) * mm, "end": v(0, 457.2) * mm});
            skLineSegment(sketch, "E130", {"start": v(0, 457.2) * mm, "end": v(127, 457.2) * mm});
            skLineSegment(sketch, "E131", {"start": v(127, 457.2) * mm, "end": v(127, 127) * mm});
            skLineSegment(sketch, "E132", {"start": v(127, 127) * mm, "end": v(457.2, 127) * mm});
            skLineSegment(sketch, "E133", {"start": v(457.2, 127) * mm, "end": v(457.2, 0) * mm});
            skLineSegment(sketch, "E134", {"start": v(457.2, 0) * mm, "end": v(0, 0) * mm});
            skLineSegment(sketch, "E135", {"start": v(7645.4, 0) * mm, "end": v(7188.2, 0) * mm});
            skLineSegment(sketch, "E136", {"start": v(7188.2, 0) * mm, "end": v(7188.2, 127) * mm});
            skLineSegment(sketch, "E137", {"start": v(7188.2, 127) * mm, "end": v(7518.4, 127) * mm});
            skLineSegment(sketch, "E138", {"start": v(7518.4, 127) * mm, "end": v(7518.4, 457.2) * mm});
            skLineSegment(sketch, "E139", {"start": v(7518.4, 457.2) * mm, "end": v(7645.4, 457.2) * mm});
            skLineSegment(sketch, "E140", {"start": v(7645.4, 457.2) * mm, "end": v(7645.4, 0) * mm});
            skLineSegment(sketch, "E141", {"start": v(10363.2, 10541) * mm, "end": v(9906, 10541) * mm});
            skLineSegment(sketch, "E142", {"start": v(9906, 10541) * mm, "end": v(9906, 10668) * mm});
            skLineSegment(sketch, "E143", {"start": v(9906, 10668) * mm, "end": v(10236.2, 10668) * mm});
            skLineSegment(sketch, "E144", {"start": v(10236.2, 10668) * mm, "end": v(10236.2, 10998.2) * mm});
            skLineSegment(sketch, "E145", {"start": v(10236.2, 10998.2) * mm, "end": v(10363.2, 10998.2) * mm});
            skLineSegment(sketch, "E146", {"start": v(10363.2, 10998.2) * mm, "end": v(10363.2, 10541) * mm});
            skLineSegment(sketch, "E147", {"start": v(10363.2, 19075.4) * mm, "end": v(10363.2, 18618.2) * mm});
            skLineSegment(sketch, "E148", {"start": v(10363.2, 18618.2) * mm, "end": v(10236.2, 18618.2) * mm});
            skLineSegment(sketch, "E149", {"start": v(10236.2, 18618.2) * mm, "end": v(10236.2, 18948.4) * mm});
            skLineSegment(sketch, "E150", {"start": v(10236.2, 18948.4) * mm, "end": v(9906, 18948.4) * mm});
            skLineSegment(sketch, "E151", {"start": v(9906, 18948.4) * mm, "end": v(9906, 19075.4) * mm});
            skLineSegment(sketch, "E152", {"start": v(9906, 19075.4) * mm, "end": v(10363.2, 19075.4) * mm});
            skLineSegment(sketch, "E153", {"start": v(0, 22885.4) * mm, "end": v(0, 23342.6) * mm});
            skLineSegment(sketch, "E154", {"start": v(0, 23342.6) * mm, "end": v(457.2, 23342.6) * mm});
            skLineSegment(sketch, "E155", {"start": v(457.2, 23342.6) * mm, "end": v(457.2, 23215.6) * mm});
            skLineSegment(sketch, "E156", {"start": v(457.2, 23215.6) * mm, "end": v(127, 23215.6) * mm});
            skLineSegment(sketch, "E157", {"start": v(127, 23215.6) * mm, "end": v(127, 22885.4) * mm});
            skLineSegment(sketch, "E158", {"start": v(127, 22885.4) * mm, "end": v(0, 22885.4) * mm});
            skLineSegment(sketch, "E159", {"start": v(5486.4, 23342.6) * mm, "end": v(5029.2, 23342.6) * mm});
            skLineSegment(sketch, "E160", {"start": v(5029.2, 23342.6) * mm, "end": v(5029.2, 23215.6) * mm});
            skLineSegment(sketch, "E161", {"start": v(5029.2, 23215.6) * mm, "end": v(5359.4, 23215.6) * mm});
            skLineSegment(sketch, "E162", {"start": v(5359.4, 23215.6) * mm, "end": v(5359.4, 22885.4) * mm});
            skLineSegment(sketch, "E163", {"start": v(5359.4, 22885.4) * mm, "end": v(5486.4, 22885.4) * mm});
            skLineSegment(sketch, "E164", {"start": v(5486.4, 22885.4) * mm, "end": v(5486.4, 23342.6) * mm});
            skSolve(sketch);
        }
        {
            var Q0;
            Q0=qSketchRegion(id+"F40",true);
            extrude(context, id + "F41", {"entities" : qUnion([Q0]), "operationType" : NewBodyOperationType.ADD, "depth" : 101.6 * mm});
        }
    });
